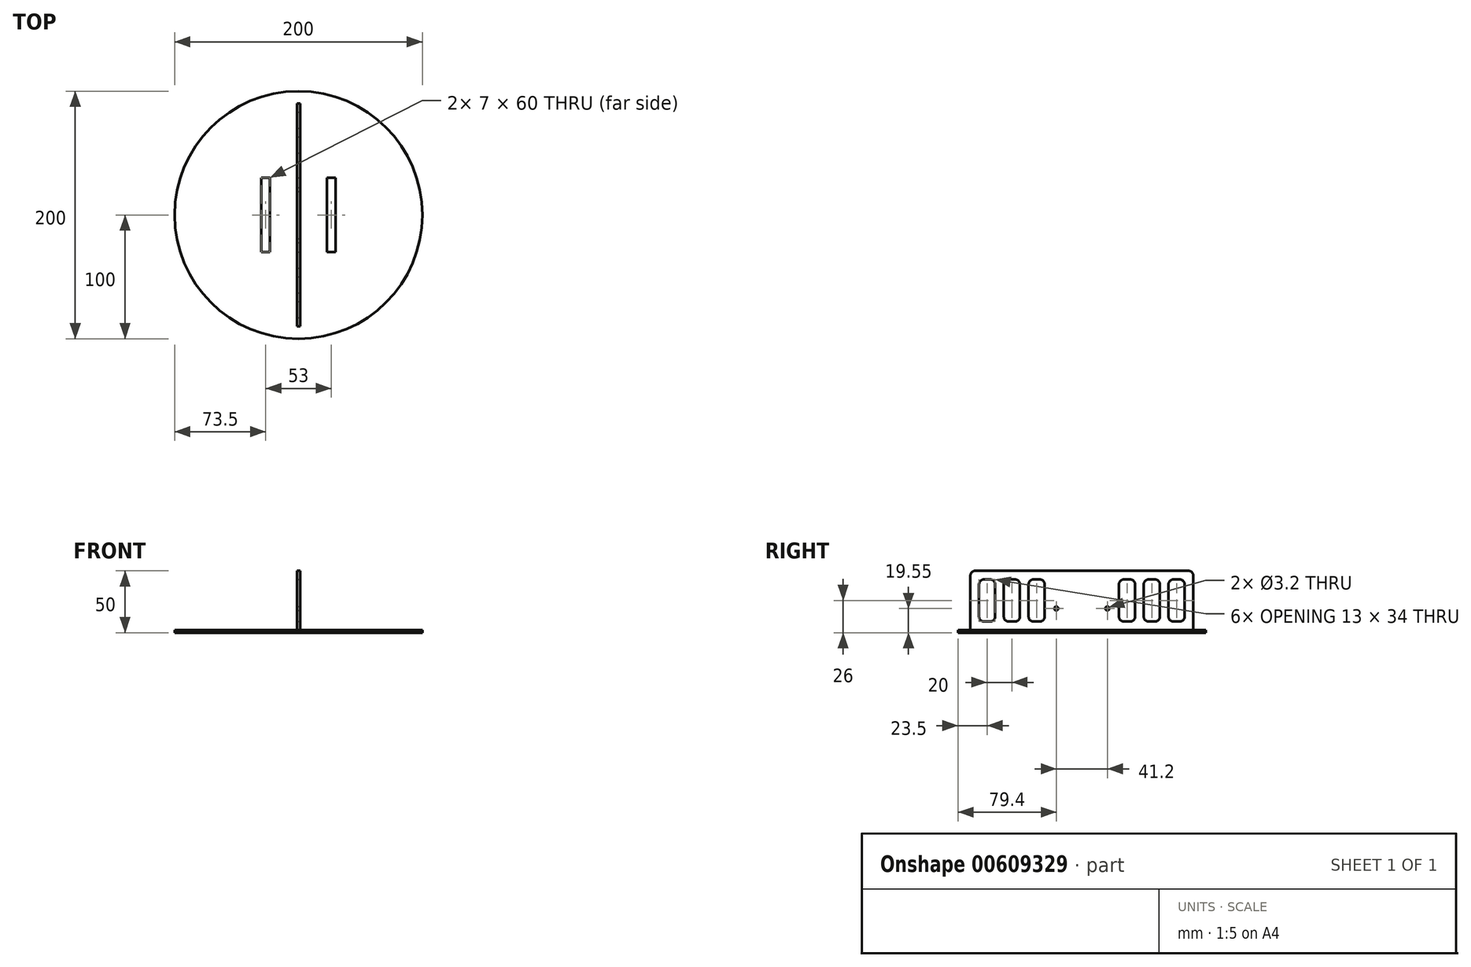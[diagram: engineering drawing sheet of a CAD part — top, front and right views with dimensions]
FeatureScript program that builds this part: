
annotation { "Feature Type Name" : "Feature", "Feature Type Description" : "" }
export const myFeature = defineFeature(function(context is Context, id is Id, definition is map)
    precondition{}
    {
        {
            var Q0;
            Q0=qCreatedBy(makeId("Top.planeOp"),FACE);
            var sketch = newSketch(context, id + "F0", { "sketchPlane" : qUnion([Q0])});
            skCircle(sketch, "E0", {"center": v(0, 0) * mm, "radius": 100 * mm});
            skLineSegment(sketch, "E1.bottom", {"start": v(-23, 30) * mm, "end": v(-30, 30) * mm});
            skLineSegment(sketch, "E1.top", {"start": v(-23, -30) * mm, "end": v(-30, -30) * mm});
            skLineSegment(sketch, "E1.left", {"start": v(-23, 30) * mm, "end": v(-23, -30) * mm});
            skLineSegment(sketch, "E1.right", {"start": v(-30, 30) * mm, "end": v(-30, -30) * mm});
            skPoint(sketch, "E1.middle", {"position": v(-26.5, 0) * mm});
            skLineSegment(sketch, "E2.MirrorCS", {"start": v(23, 30) * mm, "end": v(30, 30) * mm});
            skLineSegment(sketch, "E3.MirrorCS", {"start": v(23, 30) * mm, "end": v(23, -30) * mm});
            skLineSegment(sketch, "E4.MirrorCS", {"start": v(23, -30) * mm, "end": v(30, -30) * mm});
            skLineSegment(sketch, "E5.MirrorCS", {"start": v(30, 30) * mm, "end": v(30, -30) * mm});
            skPoint(sketch, "E6.MirrorP", {"position": v(26.5, 0) * mm});
            skLineSegment(sketch, "E7.bottom", {"start": v(1.25, 90) * mm, "end": v(-1.25, 90) * mm});
            skLineSegment(sketch, "E7.top", {"start": v(1.25, -90) * mm, "end": v(-1.25, -90) * mm});
            skLineSegment(sketch, "E7.left", {"start": v(1.25, 90) * mm, "end": v(1.25, -90) * mm});
            skLineSegment(sketch, "E7.right", {"start": v(-1.25, 90) * mm, "end": v(-1.25, -90) * mm});
            skSolve(sketch);
        }
        {
            var Q0;
            Q0=qSketchRegion(id+"F0",true);
            extrude(context, id + "F1", {"entities" : qUnion([Q0]), "depth" : 2 * mm, "offsetDistance" : 25.4 * mm});
        }
        {
            var Q0;
            Q0=makeQuery(id+"F0.imprint","IMPRINT",FACE,{"disambiguationData":[TD([[makeQuery(id+"F0.imprint","IMPRINT",EDGE,{"derivedFrom":sQuery(id+"F0.wireOp",EDGE,"E7.bottom")}),1.0]])]});
            extrude(context, id + "F2", {"entities" : qUnion([Q0]), "operationType" : NewBodyOperationType.ADD, "depth" : 50 * mm, "offsetDistance" : 25.4 * mm});
        }
        {
            var Q0;
            Q0=makeQuery(id+"F2.opExtrude","SWEPT_FACE",FACE,{"disambiguationData":[OSD([sQuery(id+"F0.wireOp",EDGE,"E7.left")])]});
            var sketch = newSketch(context, id + "F3", { "sketchPlane" : qUnion([Q0])});
            skCircle(sketch, "E8", {"center": v(-20.6, 19.55) * mm, "radius": 1.6 * mm});
            skCircle(sketch, "E9.MirrorC", {"center": v(20.6, 19.55) * mm, "radius": 1.6 * mm});
            skLineSegment(sketch, "E10.bottom", {"start": v(-83, 43) * mm, "end": v(-70, 43) * mm});
            skLineSegment(sketch, "E10.top", {"start": v(-83, 9) * mm, "end": v(-70, 9) * mm});
            skLineSegment(sketch, "E10.left", {"start": v(-83, 43) * mm, "end": v(-83, 9) * mm});
            skLineSegment(sketch, "E10.right", {"start": v(-70, 43) * mm, "end": v(-70, 9) * mm});
            skLineSegment(sketch, "E11.1.0.0", {"start": v(-63, 43) * mm, "end": v(-63, 9) * mm});
            skLineSegment(sketch, "E11.1.0.1", {"start": v(-63, 9) * mm, "end": v(-50, 9) * mm});
            skLineSegment(sketch, "E11.1.0.2", {"start": v(-50, 43) * mm, "end": v(-50, 9) * mm});
            skLineSegment(sketch, "E11.1.0.3", {"start": v(-63, 43) * mm, "end": v(-50, 43) * mm});
            skLineSegment(sketch, "E11.2.0.0", {"start": v(-43, 43) * mm, "end": v(-43, 9) * mm});
            skLineSegment(sketch, "E11.2.0.1", {"start": v(-43, 9) * mm, "end": v(-30, 9) * mm});
            skLineSegment(sketch, "E11.2.0.2", {"start": v(-30, 43) * mm, "end": v(-30, 9) * mm});
            skLineSegment(sketch, "E11.2.0.3", {"start": v(-43, 43) * mm, "end": v(-30, 43) * mm});
            skLineSegment(sketch, "E11.direction1", {"start": v(-83, 9) * mm, "end": v(-63, 9) * mm, "construction": true});
            skLineSegment(sketch, "E12.MirrorCS", {"start": v(83, 9) * mm, "end": v(70, 9) * mm});
            skLineSegment(sketch, "E13.MirrorCS", {"start": v(63, 43) * mm, "end": v(63, 9) * mm});
            skLineSegment(sketch, "E14.MirrorCS", {"start": v(43, 43) * mm, "end": v(43, 9) * mm});
            skLineSegment(sketch, "E15.MirrorCS", {"start": v(70, 43) * mm, "end": v(70, 9) * mm});
            skLineSegment(sketch, "E16.MirrorCS", {"start": v(63, 9) * mm, "end": v(50, 9) * mm});
            skLineSegment(sketch, "E17.MirrorCS", {"start": v(43, 9) * mm, "end": v(30, 9) * mm});
            skLineSegment(sketch, "E18.MirrorCS", {"start": v(83, 43) * mm, "end": v(70, 43) * mm});
            skLineSegment(sketch, "E19.MirrorCS", {"start": v(43, 43) * mm, "end": v(30, 43) * mm});
            skLineSegment(sketch, "E20.MirrorCS", {"start": v(30, 43) * mm, "end": v(30, 9) * mm});
            skLineSegment(sketch, "E21.MirrorCS", {"start": v(50, 43) * mm, "end": v(50, 9) * mm});
            skLineSegment(sketch, "E22.MirrorCS", {"start": v(63, 43) * mm, "end": v(50, 43) * mm});
            skLineSegment(sketch, "E23.MirrorCS", {"start": v(83, 9) * mm, "end": v(63, 9) * mm, "construction": true});
            skLineSegment(sketch, "E24.MirrorCS", {"start": v(83, 43) * mm, "end": v(83, 9) * mm});
            skSolve(sketch);
        }
        {
            var Q0;
            Q0=qSketchRegion(id+"F3",true);
            extrude(context, id + "F4", {"entities" : qUnion([Q0]), "operationType" : NewBodyOperationType.REMOVE, "oppositeDirection" : true, "depth" : 4 * mm, "offsetDistance" : 25.4 * mm});
        }
        {
            var Q0;
            Q0=makeQuery(id+"F2.opExtrude","CAP_EDGE",EDGE,{"disambiguationData":[OSD([sQuery(id+"F0.wireOp",EDGE,"E7.top")])],"isStart":false});
            var Q1;
            Q1=makeQuery(id+"F2.opExtrude","CAP_EDGE",EDGE,{"disambiguationData":[OSD([sQuery(id+"F0.wireOp",EDGE,"E7.bottom")])],"isStart":false});
            var Q2;
            Q2=makeQuery(id+"F4.boolean.opBoolean","COPY",EDGE,{"derivedFrom":makeQuery(id+"F4.opExtrude","SWEPT_EDGE",EDGE,{"disambiguationData":[OSD([sQuery(id+"F3.wireOp",EDGE,"E16.MirrorCS"),sQuery(id+"F3.wireOp",EDGE,"E21.MirrorCS")])]})});
            var Q3;
            Q3=makeQuery(id+"F4.boolean.opBoolean","COPY",EDGE,{"derivedFrom":makeQuery(id+"F4.opExtrude","SWEPT_EDGE",EDGE,{"disambiguationData":[OSD([sQuery(id+"F3.wireOp",EDGE,"E13.MirrorCS"),sQuery(id+"F3.wireOp",EDGE,"E16.MirrorCS")])]})});
            var Q4;
            Q4=makeQuery(id+"F4.boolean.opBoolean","COPY",EDGE,{"derivedFrom":makeQuery(id+"F4.opExtrude","SWEPT_EDGE",EDGE,{"disambiguationData":[OSD([sQuery(id+"F3.wireOp",EDGE,"E12.MirrorCS"),sQuery(id+"F3.wireOp",EDGE,"E24.MirrorCS")])]})});
            var Q5;
            Q5=makeQuery(id+"F4.boolean.opBoolean","COPY",EDGE,{"derivedFrom":makeQuery(id+"F4.opExtrude","SWEPT_EDGE",EDGE,{"disambiguationData":[OSD([sQuery(id+"F3.wireOp",EDGE,"E12.MirrorCS"),sQuery(id+"F3.wireOp",EDGE,"E15.MirrorCS")])]})});
            var Q6;
            Q6=makeQuery(id+"F4.boolean.opBoolean","COPY",EDGE,{"derivedFrom":makeQuery(id+"F4.opExtrude","SWEPT_EDGE",EDGE,{"disambiguationData":[OSD([sQuery(id+"F3.wireOp",EDGE,"E17.MirrorCS"),sQuery(id+"F3.wireOp",EDGE,"E20.MirrorCS")])]})});
            var Q7;
            Q7=makeQuery(id+"F4.boolean.opBoolean","COPY",EDGE,{"derivedFrom":makeQuery(id+"F4.opExtrude","SWEPT_EDGE",EDGE,{"disambiguationData":[OSD([sQuery(id+"F3.wireOp",EDGE,"E11.2.0.0"),sQuery(id+"F3.wireOp",EDGE,"E11.2.0.1")])]})});
            var Q8;
            Q8=makeQuery(id+"F4.boolean.opBoolean","COPY",EDGE,{"derivedFrom":makeQuery(id+"F4.opExtrude","SWEPT_EDGE",EDGE,{"disambiguationData":[OSD([sQuery(id+"F3.wireOp",EDGE,"E18.MirrorCS"),sQuery(id+"F3.wireOp",EDGE,"E24.MirrorCS")])]})});
            var Q9;
            Q9=makeQuery(id+"F4.boolean.opBoolean","COPY",EDGE,{"derivedFrom":makeQuery(id+"F4.opExtrude","SWEPT_EDGE",EDGE,{"disambiguationData":[OSD([sQuery(id+"F3.wireOp",EDGE,"E13.MirrorCS"),sQuery(id+"F3.wireOp",EDGE,"E22.MirrorCS")])]})});
            var Q10;
            Q10=makeQuery(id+"F4.boolean.opBoolean","COPY",EDGE,{"derivedFrom":makeQuery(id+"F4.opExtrude","SWEPT_EDGE",EDGE,{"disambiguationData":[OSD([sQuery(id+"F3.wireOp",EDGE,"E14.MirrorCS"),sQuery(id+"F3.wireOp",EDGE,"E19.MirrorCS")])]})});
            var Q11;
            Q11=makeQuery(id+"F4.boolean.opBoolean","COPY",EDGE,{"derivedFrom":makeQuery(id+"F4.opExtrude","SWEPT_EDGE",EDGE,{"disambiguationData":[OSD([sQuery(id+"F3.wireOp",EDGE,"E11.2.0.2"),sQuery(id+"F3.wireOp",EDGE,"E11.2.0.3")])]})});
            var Q12;
            Q12=makeQuery(id+"F4.boolean.opBoolean","COPY",EDGE,{"derivedFrom":makeQuery(id+"F4.opExtrude","SWEPT_EDGE",EDGE,{"disambiguationData":[OSD([sQuery(id+"F3.wireOp",EDGE,"E11.1.0.2"),sQuery(id+"F3.wireOp",EDGE,"E11.1.0.3")])]})});
            var Q13;
            Q13=makeQuery(id+"F4.boolean.opBoolean","COPY",EDGE,{"derivedFrom":makeQuery(id+"F4.opExtrude","SWEPT_EDGE",EDGE,{"disambiguationData":[OSD([sQuery(id+"F3.wireOp",EDGE,"E10.bottom"),sQuery(id+"F3.wireOp",EDGE,"E10.right")])]})});
            var Q14;
            Q14=makeQuery(id+"F4.boolean.opBoolean","COPY",EDGE,{"derivedFrom":makeQuery(id+"F4.opExtrude","SWEPT_EDGE",EDGE,{"disambiguationData":[OSD([sQuery(id+"F3.wireOp",EDGE,"E10.top"),sQuery(id+"F3.wireOp",EDGE,"E10.right")])]})});
            var Q15;
            Q15=makeQuery(id+"F4.boolean.opBoolean","COPY",EDGE,{"derivedFrom":makeQuery(id+"F4.opExtrude","SWEPT_EDGE",EDGE,{"disambiguationData":[OSD([sQuery(id+"F3.wireOp",EDGE,"E11.1.0.1"),sQuery(id+"F3.wireOp",EDGE,"E11.1.0.2")])]})});
            var Q16;
            Q16=makeQuery(id+"F4.boolean.opBoolean","COPY",EDGE,{"derivedFrom":makeQuery(id+"F4.opExtrude","SWEPT_EDGE",EDGE,{"disambiguationData":[OSD([sQuery(id+"F3.wireOp",EDGE,"E11.2.0.1"),sQuery(id+"F3.wireOp",EDGE,"E11.2.0.2")])]})});
            var Q17;
            Q17=makeQuery(id+"F4.boolean.opBoolean","COPY",EDGE,{"derivedFrom":makeQuery(id+"F4.opExtrude","SWEPT_EDGE",EDGE,{"disambiguationData":[OSD([sQuery(id+"F3.wireOp",EDGE,"E11.1.0.0"),sQuery(id+"F3.wireOp",EDGE,"E11.1.0.1")])]})});
            var Q18;
            Q18=makeQuery(id+"F4.boolean.opBoolean","COPY",EDGE,{"derivedFrom":makeQuery(id+"F4.opExtrude","SWEPT_EDGE",EDGE,{"disambiguationData":[OSD([sQuery(id+"F3.wireOp",EDGE,"E10.top"),sQuery(id+"F3.wireOp",EDGE,"E10.left")])]})});
            var Q19;
            Q19=makeQuery(id+"F4.boolean.opBoolean","COPY",EDGE,{"derivedFrom":makeQuery(id+"F4.opExtrude","SWEPT_EDGE",EDGE,{"disambiguationData":[OSD([sQuery(id+"F3.wireOp",EDGE,"E15.MirrorCS"),sQuery(id+"F3.wireOp",EDGE,"E18.MirrorCS")])]})});
            var Q20;
            Q20=makeQuery(id+"F4.boolean.opBoolean","COPY",EDGE,{"derivedFrom":makeQuery(id+"F4.opExtrude","SWEPT_EDGE",EDGE,{"disambiguationData":[OSD([sQuery(id+"F3.wireOp",EDGE,"E21.MirrorCS"),sQuery(id+"F3.wireOp",EDGE,"E22.MirrorCS")])]})});
            var Q21;
            Q21=makeQuery(id+"F4.boolean.opBoolean","COPY",EDGE,{"derivedFrom":makeQuery(id+"F4.opExtrude","SWEPT_EDGE",EDGE,{"disambiguationData":[OSD([sQuery(id+"F3.wireOp",EDGE,"E19.MirrorCS"),sQuery(id+"F3.wireOp",EDGE,"E20.MirrorCS")])]})});
            var Q22;
            Q22=makeQuery(id+"F4.boolean.opBoolean","COPY",EDGE,{"derivedFrom":makeQuery(id+"F4.opExtrude","SWEPT_EDGE",EDGE,{"disambiguationData":[OSD([sQuery(id+"F3.wireOp",EDGE,"E11.1.0.0"),sQuery(id+"F3.wireOp",EDGE,"E11.1.0.3")])]})});
            var Q23;
            Q23=makeQuery(id+"F4.boolean.opBoolean","COPY",EDGE,{"derivedFrom":makeQuery(id+"F4.opExtrude","SWEPT_EDGE",EDGE,{"disambiguationData":[OSD([sQuery(id+"F3.wireOp",EDGE,"E11.2.0.0"),sQuery(id+"F3.wireOp",EDGE,"E11.2.0.3")])]})});
            var Q24;
            Q24=makeQuery(id+"F4.boolean.opBoolean","COPY",EDGE,{"derivedFrom":makeQuery(id+"F4.opExtrude","SWEPT_EDGE",EDGE,{"disambiguationData":[OSD([sQuery(id+"F3.wireOp",EDGE,"E10.bottom"),sQuery(id+"F3.wireOp",EDGE,"E10.left")])]})});
            var Q25;
            Q25=makeQuery(id+"F4.boolean.opBoolean","COPY",EDGE,{"derivedFrom":makeQuery(id+"F4.opExtrude","SWEPT_EDGE",EDGE,{"disambiguationData":[OSD([sQuery(id+"F3.wireOp",EDGE,"E14.MirrorCS"),sQuery(id+"F3.wireOp",EDGE,"E17.MirrorCS")])]})});
            fillet(context, id + "F5", {"entities" : qUnion([Q0, Q1, Q2, Q3, Q4, Q5, Q6, Q7, Q8, Q9, Q10, Q11, Q12, Q13, Q14, Q15, Q16, Q17, Q18, Q19, Q20, Q21, Q22, Q23, Q24, Q25]), "radius" : 4 * mm, "tangentPropagation" : true, "allowEdgeOverflow" : false});
        }
    });
